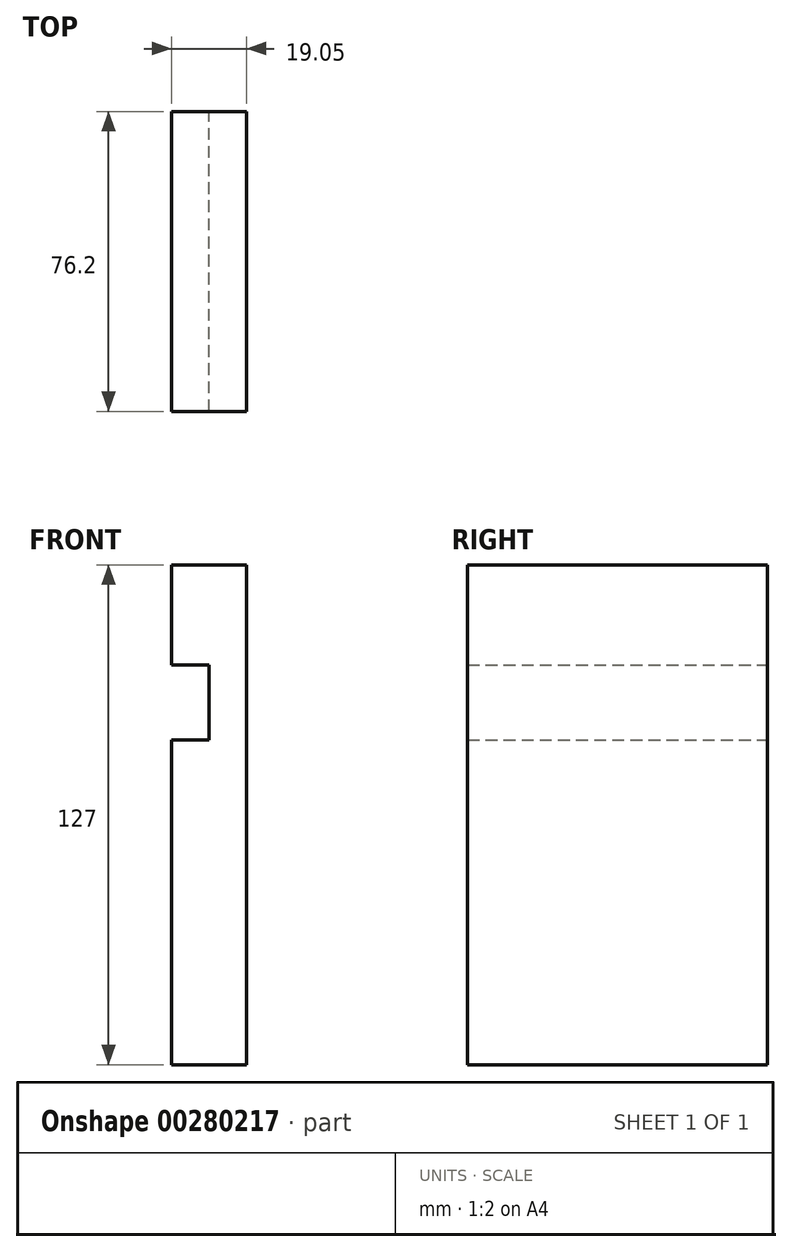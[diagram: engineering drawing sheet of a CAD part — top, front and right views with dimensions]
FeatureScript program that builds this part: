
annotation { "Feature Type Name" : "Feature", "Feature Type Description" : "" }
export const myFeature = defineFeature(function(context is Context, id is Id, definition is map)
    precondition{}
    {
        {
            var Q0;
            Q0=qCreatedBy(makeId("Front.planeOp"),FACE);
            var sketch = newSketch(context, id + "F0", { "sketchPlane" : qUnion([Q0])});
            skLineSegment(sketch, "E0", {"start": v(10.36, 39.36) * mm, "end": v(29.4, 39.36) * mm});
            skLineSegment(sketch, "E1", {"start": v(29.4, 39.36) * mm, "end": v(29.4, -87.64) * mm});
            skLineSegment(sketch, "E2", {"start": v(29.4, -87.64) * mm, "end": v(10.36, -87.64) * mm});
            skLineSegment(sketch, "E3", {"start": v(10.36, 39.36) * mm, "end": v(10.36, 13.96) * mm});
            skLineSegment(sketch, "E4", {"start": v(10.36, 13.96) * mm, "end": v(19.88, 13.96) * mm});
            skLineSegment(sketch, "E5", {"start": v(19.88, 13.96) * mm, "end": v(19.88, -5.09) * mm});
            skLineSegment(sketch, "E6", {"start": v(19.88, -5.09) * mm, "end": v(10.36, -5.09) * mm});
            skLineSegment(sketch, "E7", {"start": v(10.36, -5.09) * mm, "end": v(10.36, -87.64) * mm});
            skSolve(sketch);
        }
        {
            var Q0;
            Q0=makeQuery(id+"F0.imprint","IMPRINT",FACE,{"disambiguationData":[TD([[makeQuery(id+"F0.imprint","IMPRINT",EDGE,{"derivedFrom":sQuery(id+"F0.wireOp",EDGE,"E0")}),-1.0]])]});
            extrude(context, id + "F1", {"entities" : qUnion([Q0]), "depth" : 76.2 * mm});
        }
    });
